# Revit family: xFaucet-Single-American_Standard-Patience-7106.152
name_source: partatom
category: Plumbing Fixtures
revit_build: Autodesk Revit 2014 (Build: 20130308_1515(x64)
units: mm (PartAtom-declared; Revit-internal decimal feet)

## types (1)
- 7106.152
    ADA Compliant = Yes
    Assembly Code = D2020300
    CW Connection = Yes
    CWFU = 1.5
    Cold Water Connection Diameter = 3/8"
    Default Elevation = 0"
    Description = Patience Single Control Vessel Faucet. Grid Drain.
    Finish = Brass-American Standard-002-Polished Chrome
    Flow Rate = 1.2 gpm (4.5 L/min)
    HW Connection = Yes
    HWFU = 1.5
    Height = 14 3/8"
    Hot Water Connection Diameter = 3/8"
    Installation Type = Deck Mounted
    Length = 7 1/4"
    Manufacturer = American Standard
    Material = Brass-American Standard-002-Polished Chrome
    Model = 7106.152
    Price = Prices may vary. Please consult Manufacturer Representative for most up-to-date price list.
    Product Documentation Link = https://www.americanstandard-us.com
    Product Page URL = https://www.americanstandard-us.com
    Specification = Single control lavatory faucet shall feature a brass body and metal lever handle. Fitting shall be equipped with flexible supplies with 3/8in compression connectors. Shall also feature washerless ceramic disc valve cartridge with an integral hot limit safety stop. Fitting shall be American Standard Model 7106.152
    URL = https://www.americanstandard-us.com
    Vent Connection = No
    WFU = 2
    Warranty Information = Limited Lifetime Function and Finish Warranty
    Waste Connection = Yes
    Width = 5 1/2"

## geometry (parser evidence)
native form markers: Sweep x1
no freeform markers — native parametric forms only
